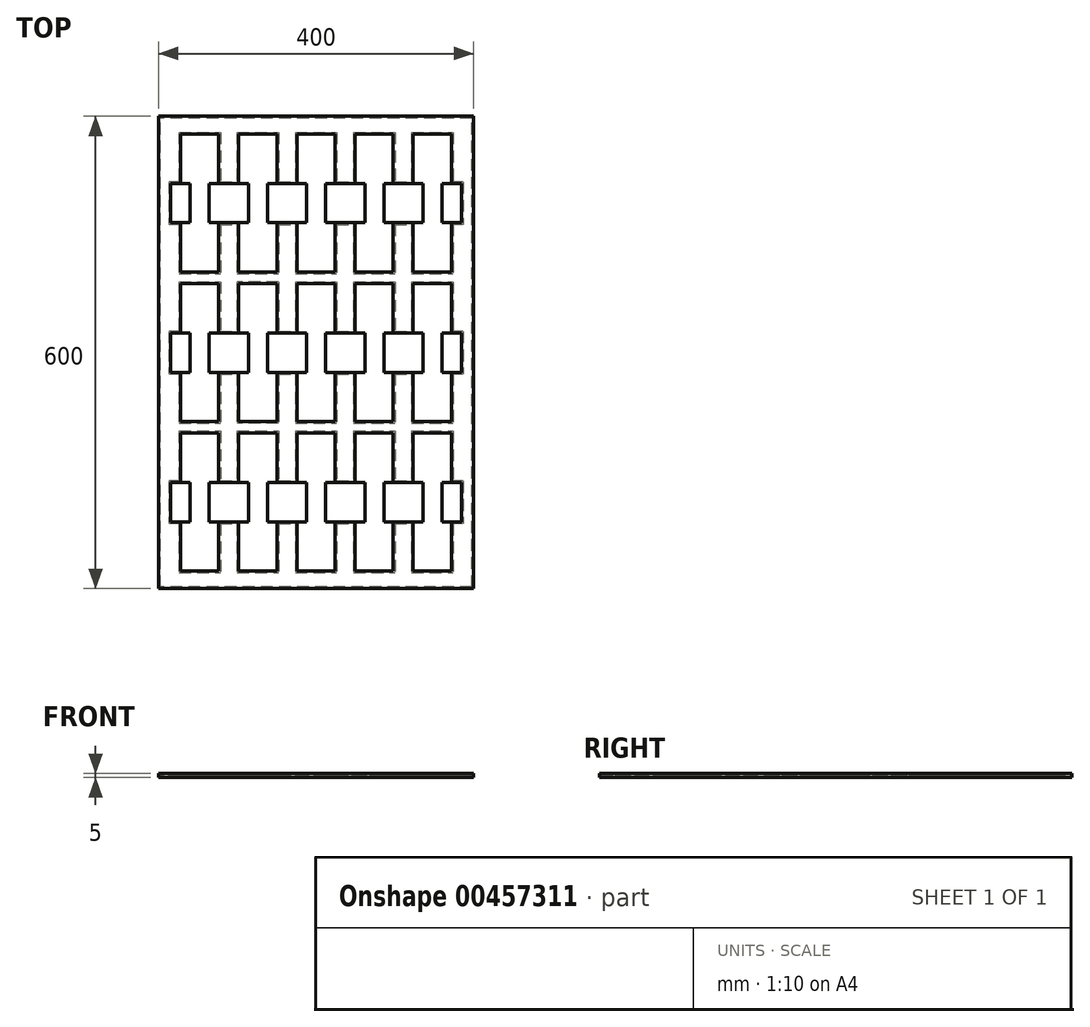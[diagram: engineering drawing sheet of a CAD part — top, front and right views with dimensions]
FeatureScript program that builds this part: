
annotation { "Feature Type Name" : "Feature", "Feature Type Description" : "" }
export const myFeature = defineFeature(function(context is Context, id is Id, definition is map)
    precondition{}
    {
        {
            var Q0;
            Q0=qCreatedBy(makeId("Top.planeOp"),FACE);
            var sketch = newSketch(context, id + "F0", { "sketchPlane" : qUnion([Q0])});
            skLineSegment(sketch, "E0.bottom", {"start": v(200, -300) * mm, "end": v(-200, -300) * mm});
            skLineSegment(sketch, "E0.top", {"start": v(200, 300) * mm, "end": v(-200, 300) * mm});
            skLineSegment(sketch, "E0.left", {"start": v(200, -300) * mm, "end": v(200, 300) * mm});
            skLineSegment(sketch, "E0.right", {"start": v(-200, -300) * mm, "end": v(-200, 300) * mm});
            skPoint(sketch, "E0.middle", {"position": v(0, 0) * mm});
            skSolve(sketch);
        }
        {
            var Q0;
            Q0 = qSketchRegion(id + "F0", true);
            extrude(context, id + "F1", {"entities" : qUnion([Q0]), "depth" : 2 * mm});
        }
        {
            var Q0;
            Q0=makeQuery(id+"F1.opExtrude","CAP_FACE",FACE,{"disambiguationData":[OSD([sQuery(id+"F0.wireOp",EDGE,"E0.bottom"),sQuery(id+"F0.wireOp",EDGE,"E0.top"),sQuery(id+"F0.wireOp",EDGE,"E0.left"),sQuery(id+"F0.wireOp",EDGE,"E0.right")])],"isStart":false});
            var sketch = newSketch(context, id + "F2", { "sketchPlane" : qUnion([Q0])});
            skLineSegment(sketch, "E1.bottom", {"start": v(-172, 277.5) * mm, "end": v(-123.5, 277.5) * mm});
            skLineSegment(sketch, "E1.top", {"start": v(-172, 102) * mm, "end": v(-123.5, 102) * mm});
            skLineSegment(sketch, "E1.left", {"start": v(-172, 277.5) * mm, "end": v(-172, 102) * mm});
            skLineSegment(sketch, "E1.right", {"start": v(-123.5, 277.5) * mm, "end": v(-123.5, 102) * mm});
            skLineSegment(sketch, "E2.0.1.0", {"start": v(-172, 87.75) * mm, "end": v(-123.5, 87.75) * mm});
            skLineSegment(sketch, "E2.0.1.1", {"start": v(-123.5, 87.75) * mm, "end": v(-123.5, -87.75) * mm});
            skLineSegment(sketch, "E2.0.1.2", {"start": v(-172, -87.75) * mm, "end": v(-123.5, -87.75) * mm});
            skLineSegment(sketch, "E2.0.1.3", {"start": v(-172, 87.75) * mm, "end": v(-172, -87.75) * mm});
            skLineSegment(sketch, "E2.0.2.0", {"start": v(-172, -102) * mm, "end": v(-123.5, -102) * mm});
            skLineSegment(sketch, "E2.0.2.1", {"start": v(-123.5, -102) * mm, "end": v(-123.5, -277.5) * mm});
            skLineSegment(sketch, "E2.0.2.2", {"start": v(-172, -277.5) * mm, "end": v(-123.5, -277.5) * mm});
            skLineSegment(sketch, "E2.0.2.3", {"start": v(-172, -102) * mm, "end": v(-172, -277.5) * mm});
            skLineSegment(sketch, "E2.1.0.0", {"start": v(-98.13, 277.5) * mm, "end": v(-49.63, 277.5) * mm});
            skLineSegment(sketch, "E2.1.0.1", {"start": v(-49.63, 277.5) * mm, "end": v(-49.63, 102) * mm});
            skLineSegment(sketch, "E2.1.0.2", {"start": v(-98.13, 102) * mm, "end": v(-49.63, 102) * mm});
            skLineSegment(sketch, "E2.1.0.3", {"start": v(-98.13, 277.5) * mm, "end": v(-98.13, 102) * mm});
            skLineSegment(sketch, "E2.1.1.0", {"start": v(-98.13, 87.75) * mm, "end": v(-49.63, 87.75) * mm});
            skLineSegment(sketch, "E2.1.1.1", {"start": v(-49.63, 87.75) * mm, "end": v(-49.63, -87.75) * mm});
            skLineSegment(sketch, "E2.1.1.2", {"start": v(-98.13, -87.75) * mm, "end": v(-49.63, -87.75) * mm});
            skLineSegment(sketch, "E2.1.1.3", {"start": v(-98.13, 87.75) * mm, "end": v(-98.13, -87.75) * mm});
            skLineSegment(sketch, "E2.1.2.0", {"start": v(-98.13, -102) * mm, "end": v(-49.63, -102) * mm});
            skLineSegment(sketch, "E2.1.2.1", {"start": v(-49.63, -102) * mm, "end": v(-49.63, -277.5) * mm});
            skLineSegment(sketch, "E2.1.2.2", {"start": v(-98.13, -277.5) * mm, "end": v(-49.63, -277.5) * mm});
            skLineSegment(sketch, "E2.1.2.3", {"start": v(-98.13, -102) * mm, "end": v(-98.13, -277.5) * mm});
            skLineSegment(sketch, "E2.2.0.0", {"start": v(-24.25, 277.5) * mm, "end": v(24.25, 277.5) * mm});
            skLineSegment(sketch, "E2.2.0.1", {"start": v(24.25, 277.5) * mm, "end": v(24.25, 102) * mm});
            skLineSegment(sketch, "E2.2.0.2", {"start": v(-24.25, 102) * mm, "end": v(24.25, 102) * mm});
            skLineSegment(sketch, "E2.2.0.3", {"start": v(-24.25, 277.5) * mm, "end": v(-24.25, 102) * mm});
            skLineSegment(sketch, "E2.2.1.0", {"start": v(-24.25, 87.75) * mm, "end": v(24.25, 87.75) * mm});
            skLineSegment(sketch, "E2.2.1.1", {"start": v(24.25, 87.75) * mm, "end": v(24.25, -87.75) * mm});
            skLineSegment(sketch, "E2.2.1.2", {"start": v(-24.25, -87.75) * mm, "end": v(24.25, -87.75) * mm});
            skLineSegment(sketch, "E2.2.1.3", {"start": v(-24.25, 87.75) * mm, "end": v(-24.25, -87.75) * mm});
            skLineSegment(sketch, "E2.2.2.0", {"start": v(-24.25, -102) * mm, "end": v(24.25, -102) * mm});
            skLineSegment(sketch, "E2.2.2.1", {"start": v(24.25, -102) * mm, "end": v(24.25, -277.5) * mm});
            skLineSegment(sketch, "E2.2.2.2", {"start": v(-24.25, -277.5) * mm, "end": v(24.25, -277.5) * mm});
            skLineSegment(sketch, "E2.2.2.3", {"start": v(-24.25, -102) * mm, "end": v(-24.25, -277.5) * mm});
            skLineSegment(sketch, "E2.3.0.0", {"start": v(49.62, 277.5) * mm, "end": v(98.12, 277.5) * mm});
            skLineSegment(sketch, "E2.3.0.1", {"start": v(98.12, 277.5) * mm, "end": v(98.12, 102) * mm});
            skLineSegment(sketch, "E2.3.0.2", {"start": v(49.62, 102) * mm, "end": v(98.12, 102) * mm});
            skLineSegment(sketch, "E2.3.0.3", {"start": v(49.62, 277.5) * mm, "end": v(49.62, 102) * mm});
            skLineSegment(sketch, "E2.3.1.0", {"start": v(49.62, 87.75) * mm, "end": v(98.12, 87.75) * mm});
            skLineSegment(sketch, "E2.3.1.1", {"start": v(98.12, 87.75) * mm, "end": v(98.12, -87.75) * mm});
            skLineSegment(sketch, "E2.3.1.2", {"start": v(49.62, -87.75) * mm, "end": v(98.12, -87.75) * mm});
            skLineSegment(sketch, "E2.3.1.3", {"start": v(49.62, 87.75) * mm, "end": v(49.62, -87.75) * mm});
            skLineSegment(sketch, "E2.3.2.0", {"start": v(49.62, -102) * mm, "end": v(98.12, -102) * mm});
            skLineSegment(sketch, "E2.3.2.1", {"start": v(98.12, -102) * mm, "end": v(98.12, -277.5) * mm});
            skLineSegment(sketch, "E2.3.2.2", {"start": v(49.62, -277.5) * mm, "end": v(98.12, -277.5) * mm});
            skLineSegment(sketch, "E2.3.2.3", {"start": v(49.62, -102) * mm, "end": v(49.62, -277.5) * mm});
            skLineSegment(sketch, "E2.4.0.0", {"start": v(123.5, 277.5) * mm, "end": v(172, 277.5) * mm});
            skLineSegment(sketch, "E2.4.0.1", {"start": v(172, 277.5) * mm, "end": v(172, 102) * mm});
            skLineSegment(sketch, "E2.4.0.2", {"start": v(123.5, 102) * mm, "end": v(172, 102) * mm});
            skLineSegment(sketch, "E2.4.0.3", {"start": v(123.5, 277.5) * mm, "end": v(123.5, 102) * mm});
            skLineSegment(sketch, "E2.4.1.0", {"start": v(123.5, 87.75) * mm, "end": v(172, 87.75) * mm});
            skLineSegment(sketch, "E2.4.1.1", {"start": v(172, 87.75) * mm, "end": v(172, -87.75) * mm});
            skLineSegment(sketch, "E2.4.1.2", {"start": v(123.5, -87.75) * mm, "end": v(172, -87.75) * mm});
            skLineSegment(sketch, "E2.4.1.3", {"start": v(123.5, 87.75) * mm, "end": v(123.5, -87.75) * mm});
            skLineSegment(sketch, "E2.4.2.0", {"start": v(123.5, -102) * mm, "end": v(172, -102) * mm});
            skLineSegment(sketch, "E2.4.2.1", {"start": v(172, -102) * mm, "end": v(172, -277.5) * mm});
            skLineSegment(sketch, "E2.4.2.2", {"start": v(123.5, -277.5) * mm, "end": v(172, -277.5) * mm});
            skLineSegment(sketch, "E2.4.2.3", {"start": v(123.5, -102) * mm, "end": v(123.5, -277.5) * mm});
            skLineSegment(sketch, "E3", {"start": v(-333.48, 0) * mm, "end": v(360.99, 0) * mm, "construction": true});
            skLineSegment(sketch, "E4", {"start": v(0, 318.35) * mm, "end": v(-24.25, -9048.14) * mm, "construction": true});
            skLineSegment(sketch, "E5.bottom", {"start": v(-200, 300) * mm, "end": v(200, 300) * mm});
            skLineSegment(sketch, "E5.top", {"start": v(-200, -300) * mm, "end": v(200, -300) * mm});
            skLineSegment(sketch, "E5.left", {"start": v(-200, 300) * mm, "end": v(-200, -300) * mm});
            skLineSegment(sketch, "E5.right", {"start": v(200, 300) * mm, "end": v(200, -300) * mm});
            skSolve(sketch);
        }
        {
            var Q0;
            Q0 = qSketchRegion(id + "F2", true);
            extrude(context, id + "F3", {"entities" : qUnion([Q0]), "operationType" : NewBodyOperationType.ADD, "depth" : 3 * mm});
        }
        {
            var Q0;
            Q0=makeQuery(id+"F3.opExtrude","CAP_FACE",FACE,{"disambiguationData":[OSD([sQuery(id+"F2.wireOp",EDGE,"E1.top"),sQuery(id+"F2.wireOp",EDGE,"E1.right"),sQuery(id+"F2.wireOp",EDGE,"E2.0.1.0"),sQuery(id+"F2.wireOp",EDGE,"E2.0.1.1"),sQuery(id+"F2.wireOp",EDGE,"E2.0.1.2"),sQuery(id+"F2.wireOp",EDGE,"E2.0.1.3"),sQuery(id+"F2.wireOp",EDGE,"E2.0.2.0"),sQuery(id+"F2.wireOp",EDGE,"E2.0.2.1"),sQuery(id+"F2.wireOp",EDGE,"E2.0.2.2"),sQuery(id+"F2.wireOp",EDGE,"E2.0.2.3"),sQuery(id+"F2.wireOp",EDGE,"E2.1.0.0"),sQuery(id+"F2.wireOp",EDGE,"E2.1.0.1"),sQuery(id+"F2.wireOp",EDGE,"E2.1.0.2"),sQuery(id+"F2.wireOp",EDGE,"E2.1.0.3"),sQuery(id+"F2.wireOp",EDGE,"E2.1.1.0"),sQuery(id+"F2.wireOp",EDGE,"E2.1.1.1"),sQuery(id+"F2.wireOp",EDGE,"E2.1.1.2"),sQuery(id+"F2.wireOp",EDGE,"E2.1.1.3"),sQuery(id+"F2.wireOp",EDGE,"E2.1.2.0"),sQuery(id+"F2.wireOp",EDGE,"E2.1.2.1"),sQuery(id+"F2.wireOp",EDGE,"E2.1.2.2"),sQuery(id+"F2.wireOp",EDGE,"E2.1.2.3"),sQuery(id+"F2.wireOp",EDGE,"E2.2.0.0"),sQuery(id+"F2.wireOp",EDGE,"E2.2.0.1"),sQuery(id+"F2.wireOp",EDGE,"E2.2.0.2"),sQuery(id+"F2.wireOp",EDGE,"E2.2.0.3"),sQuery(id+"F2.wireOp",EDGE,"E2.2.1.0"),sQuery(id+"F2.wireOp",EDGE,"E2.2.1.1"),sQuery(id+"F2.wireOp",EDGE,"E2.2.1.2"),sQuery(id+"F2.wireOp",EDGE,"E2.2.1.3"),sQuery(id+"F2.wireOp",EDGE,"E2.2.2.0"),sQuery(id+"F2.wireOp",EDGE,"E2.2.2.1"),sQuery(id+"F2.wireOp",EDGE,"E2.2.2.2"),sQuery(id+"F2.wireOp",EDGE,"E2.2.2.3"),sQuery(id+"F2.wireOp",EDGE,"E2.3.0.0"),sQuery(id+"F2.wireOp",EDGE,"E2.3.0.1"),sQuery(id+"F2.wireOp",EDGE,"E2.3.0.2"),sQuery(id+"F2.wireOp",EDGE,"E2.3.0.3"),sQuery(id+"F2.wireOp",EDGE,"E2.3.1.0"),sQuery(id+"F2.wireOp",EDGE,"E2.3.1.1"),sQuery(id+"F2.wireOp",EDGE,"E2.3.1.2"),sQuery(id+"F2.wireOp",EDGE,"E2.3.1.3"),sQuery(id+"F2.wireOp",EDGE,"E2.3.2.0"),sQuery(id+"F2.wireOp",EDGE,"E2.3.2.1"),sQuery(id+"F2.wireOp",EDGE,"E2.3.2.2"),sQuery(id+"F2.wireOp",EDGE,"E2.3.2.3"),sQuery(id+"F2.wireOp",EDGE,"E2.4.0.0"),sQuery(id+"F2.wireOp",EDGE,"E2.4.0.1"),sQuery(id+"F2.wireOp",EDGE,"E2.4.0.2"),sQuery(id+"F2.wireOp",EDGE,"E2.4.0.3"),sQuery(id+"F2.wireOp",EDGE,"E2.4.1.0"),sQuery(id+"F2.wireOp",EDGE,"E2.4.1.1"),sQuery(id+"F2.wireOp",EDGE,"E2.4.1.2"),sQuery(id+"F2.wireOp",EDGE,"E2.4.1.3"),sQuery(id+"F2.wireOp",EDGE,"E2.4.2.0"),sQuery(id+"F2.wireOp",EDGE,"E2.4.2.1"),sQuery(id+"F2.wireOp",EDGE,"E2.4.2.2"),sQuery(id+"F2.wireOp",EDGE,"E2.4.2.3"),sQuery(id+"F2.wireOp",EDGE,"E1.bottom"),sQuery(id+"F2.wireOp",EDGE,"E1.left"),sQuery(id+"F2.wireOp",EDGE,"E5.bottom"),sQuery(id+"F2.wireOp",EDGE,"E5.top"),sQuery(id+"F2.wireOp",EDGE,"E5.left"),sQuery(id+"F2.wireOp",EDGE,"E5.right")])],"isStart":false});
            var sketch = newSketch(context, id + "F4", { "sketchPlane" : qUnion([Q0])});
            skLineSegment(sketch, "E6.bottom", {"start": v(-135.81, 164.75) * mm, "end": v(-85.81, 164.75) * mm});
            skLineSegment(sketch, "E6.top", {"start": v(-135.81, 214.75) * mm, "end": v(-85.81, 214.75) * mm});
            skLineSegment(sketch, "E6.left", {"start": v(-135.81, 164.75) * mm, "end": v(-135.81, 214.75) * mm});
            skLineSegment(sketch, "E6.right", {"start": v(-85.81, 164.75) * mm, "end": v(-85.81, 214.75) * mm});
            skLineSegment(sketch, "E7", {"start": v(-110.81, 237.25) * mm, "end": v(-110.81, 132.57) * mm, "construction": true});
            skLineSegment(sketch, "E8", {"start": v(-222.43, 189.75) * mm, "end": v(260.4, 189.75) * mm, "construction": true});
            skPoint(sketch, "E8.endSnap0", {"position": v(-98.13, 189.75) * mm});
            skLineSegment(sketch, "E9", {"start": v(-36.94, 239.15) * mm, "end": v(-36.94, 137.64) * mm, "construction": true});
            skLineSegment(sketch, "E10", {"start": v(-262.44, 94.87) * mm, "end": v(281.55, 94.87) * mm, "construction": true});
            skLineSegment(sketch, "E11", {"start": v(-247.35, -94.88) * mm, "end": v(283.81, -94.87) * mm, "construction": true});
            skLineSegment(sketch, "E12.0.1.0", {"start": v(-85.81, -25.25) * mm, "end": v(-85.81, 24.75) * mm});
            skLineSegment(sketch, "E12.0.1.1", {"start": v(-135.81, 24.75) * mm, "end": v(-85.81, 24.75) * mm});
            skLineSegment(sketch, "E12.0.1.2", {"start": v(-135.81, -25.25) * mm, "end": v(-135.81, 24.75) * mm});
            skLineSegment(sketch, "E12.0.1.3", {"start": v(-110.81, 47.25) * mm, "end": v(-110.81, -57.43) * mm, "construction": true});
            skLineSegment(sketch, "E12.0.1.4", {"start": v(-135.81, -25.25) * mm, "end": v(-85.81, -25.25) * mm});
            skLineSegment(sketch, "E12.0.2.0", {"start": v(-85.81, -215.25) * mm, "end": v(-85.81, -165.25) * mm});
            skLineSegment(sketch, "E12.0.2.1", {"start": v(-135.81, -165.25) * mm, "end": v(-85.81, -165.25) * mm});
            skLineSegment(sketch, "E12.0.2.2", {"start": v(-135.81, -215.25) * mm, "end": v(-135.81, -165.25) * mm});
            skLineSegment(sketch, "E12.0.2.3", {"start": v(-110.81, -142.75) * mm, "end": v(-110.81, -247.43) * mm, "construction": true});
            skLineSegment(sketch, "E12.0.2.4", {"start": v(-135.81, -215.25) * mm, "end": v(-85.81, -215.25) * mm});
            skLineSegment(sketch, "E12.1.0.0", {"start": v(-11.81, 164.75) * mm, "end": v(-11.81, 214.75) * mm});
            skLineSegment(sketch, "E12.1.0.1", {"start": v(-61.81, 214.75) * mm, "end": v(-11.81, 214.75) * mm});
            skLineSegment(sketch, "E12.1.0.2", {"start": v(-61.81, 164.75) * mm, "end": v(-61.81, 214.75) * mm});
            skLineSegment(sketch, "E12.1.0.3", {"start": v(-36.81, 237.25) * mm, "end": v(-36.81, 132.57) * mm, "construction": true});
            skLineSegment(sketch, "E12.1.0.4", {"start": v(-61.81, 164.75) * mm, "end": v(-11.81, 164.75) * mm});
            skLineSegment(sketch, "E12.1.1.0", {"start": v(-11.81, -25.25) * mm, "end": v(-11.81, 24.75) * mm});
            skLineSegment(sketch, "E12.1.1.1", {"start": v(-61.81, 24.75) * mm, "end": v(-11.81, 24.75) * mm});
            skLineSegment(sketch, "E12.1.1.2", {"start": v(-61.81, -25.25) * mm, "end": v(-61.81, 24.75) * mm});
            skLineSegment(sketch, "E12.1.1.3", {"start": v(-36.81, 47.25) * mm, "end": v(-36.81, -57.43) * mm, "construction": true});
            skLineSegment(sketch, "E12.1.1.4", {"start": v(-61.81, -25.25) * mm, "end": v(-11.81, -25.25) * mm});
            skLineSegment(sketch, "E12.1.2.0", {"start": v(-11.81, -215.25) * mm, "end": v(-11.81, -165.25) * mm});
            skLineSegment(sketch, "E12.1.2.1", {"start": v(-61.81, -165.25) * mm, "end": v(-11.81, -165.25) * mm});
            skLineSegment(sketch, "E12.1.2.2", {"start": v(-61.81, -215.25) * mm, "end": v(-61.81, -165.25) * mm});
            skLineSegment(sketch, "E12.1.2.3", {"start": v(-36.81, -142.75) * mm, "end": v(-36.81, -247.43) * mm, "construction": true});
            skLineSegment(sketch, "E12.1.2.4", {"start": v(-61.81, -215.25) * mm, "end": v(-11.81, -215.25) * mm});
            skLineSegment(sketch, "E12.2.0.0", {"start": v(62.19, 164.75) * mm, "end": v(62.19, 214.75) * mm});
            skLineSegment(sketch, "E12.2.0.1", {"start": v(12.19, 214.75) * mm, "end": v(62.19, 214.75) * mm});
            skLineSegment(sketch, "E12.2.0.2", {"start": v(12.19, 164.75) * mm, "end": v(12.19, 214.75) * mm});
            skLineSegment(sketch, "E12.2.0.3", {"start": v(37.19, 237.25) * mm, "end": v(37.19, 132.57) * mm, "construction": true});
            skLineSegment(sketch, "E12.2.0.4", {"start": v(12.19, 164.75) * mm, "end": v(62.19, 164.75) * mm});
            skLineSegment(sketch, "E12.2.1.0", {"start": v(62.19, -25.25) * mm, "end": v(62.19, 24.75) * mm});
            skLineSegment(sketch, "E12.2.1.1", {"start": v(12.19, 24.75) * mm, "end": v(62.19, 24.75) * mm});
            skLineSegment(sketch, "E12.2.1.2", {"start": v(12.19, -25.25) * mm, "end": v(12.19, 24.75) * mm});
            skLineSegment(sketch, "E12.2.1.3", {"start": v(37.19, 47.25) * mm, "end": v(37.19, -57.43) * mm, "construction": true});
            skLineSegment(sketch, "E12.2.1.4", {"start": v(12.19, -25.25) * mm, "end": v(62.19, -25.25) * mm});
            skLineSegment(sketch, "E12.2.2.0", {"start": v(62.19, -215.25) * mm, "end": v(62.19, -165.25) * mm});
            skLineSegment(sketch, "E12.2.2.1", {"start": v(12.19, -165.25) * mm, "end": v(62.19, -165.25) * mm});
            skLineSegment(sketch, "E12.2.2.2", {"start": v(12.19, -215.25) * mm, "end": v(12.19, -165.25) * mm});
            skLineSegment(sketch, "E12.2.2.3", {"start": v(37.19, -142.75) * mm, "end": v(37.19, -247.43) * mm, "construction": true});
            skLineSegment(sketch, "E12.2.2.4", {"start": v(12.19, -215.25) * mm, "end": v(62.19, -215.25) * mm});
            skLineSegment(sketch, "E12.3.0.0", {"start": v(136.19, 164.75) * mm, "end": v(136.19, 214.75) * mm});
            skLineSegment(sketch, "E12.3.0.1", {"start": v(86.19, 214.75) * mm, "end": v(136.19, 214.75) * mm});
            skLineSegment(sketch, "E12.3.0.2", {"start": v(86.19, 164.75) * mm, "end": v(86.19, 214.75) * mm});
            skLineSegment(sketch, "E12.3.0.3", {"start": v(111.19, 237.25) * mm, "end": v(111.19, 132.57) * mm, "construction": true});
            skLineSegment(sketch, "E12.3.0.4", {"start": v(86.19, 164.75) * mm, "end": v(136.19, 164.75) * mm});
            skLineSegment(sketch, "E12.3.1.0", {"start": v(136.19, -25.25) * mm, "end": v(136.19, 24.75) * mm});
            skLineSegment(sketch, "E12.3.1.1", {"start": v(86.19, 24.75) * mm, "end": v(136.19, 24.75) * mm});
            skLineSegment(sketch, "E12.3.1.2", {"start": v(86.19, -25.25) * mm, "end": v(86.19, 24.75) * mm});
            skLineSegment(sketch, "E12.3.1.3", {"start": v(111.19, 47.25) * mm, "end": v(111.19, -57.43) * mm, "construction": true});
            skLineSegment(sketch, "E12.3.1.4", {"start": v(86.19, -25.25) * mm, "end": v(136.19, -25.25) * mm});
            skLineSegment(sketch, "E12.3.2.0", {"start": v(136.19, -215.25) * mm, "end": v(136.19, -165.25) * mm});
            skLineSegment(sketch, "E12.3.2.1", {"start": v(86.19, -165.25) * mm, "end": v(136.19, -165.25) * mm});
            skLineSegment(sketch, "E12.3.2.2", {"start": v(86.19, -215.25) * mm, "end": v(86.19, -165.25) * mm});
            skLineSegment(sketch, "E12.3.2.3", {"start": v(111.19, -142.75) * mm, "end": v(111.19, -247.43) * mm, "construction": true});
            skLineSegment(sketch, "E12.3.2.4", {"start": v(86.19, -215.25) * mm, "end": v(136.19, -215.25) * mm});
            skLineSegment(sketch, "E12.direction1", {"start": v(-85.81, 164.75) * mm, "end": v(-11.81, 164.75) * mm, "construction": true});
            skLineSegment(sketch, "E12.direction2", {"start": v(-85.81, 164.75) * mm, "end": v(-85.81, -25.25) * mm, "construction": true});
            skLineSegment(sketch, "E13.bottom", {"start": v(-159.69, 214.75) * mm, "end": v(-184.69, 214.75) * mm});
            skLineSegment(sketch, "E13.top", {"start": v(-159.69, 164.75) * mm, "end": v(-184.69, 164.75) * mm});
            skLineSegment(sketch, "E13.left", {"start": v(-159.69, 214.75) * mm, "end": v(-159.69, 164.75) * mm});
            skLineSegment(sketch, "E13.right", {"start": v(-184.69, 214.75) * mm, "end": v(-184.69, 164.75) * mm});
            skLineSegment(sketch, "E14", {"start": v(-147.75, 140.31) * mm, "end": v(-147.75, 261.03) * mm, "construction": true});
            skLineSegment(sketch, "E15.0.1.0", {"start": v(-159.69, -25.25) * mm, "end": v(-184.69, -25.25) * mm});
            skLineSegment(sketch, "E15.0.1.1", {"start": v(-159.69, 24.75) * mm, "end": v(-184.69, 24.75) * mm});
            skLineSegment(sketch, "E15.0.1.2", {"start": v(-159.69, 24.75) * mm, "end": v(-159.69, -25.25) * mm});
            skLineSegment(sketch, "E15.0.1.3", {"start": v(-184.69, 24.75) * mm, "end": v(-184.69, -25.25) * mm});
            skLineSegment(sketch, "E15.1.0.0", {"start": v(185, 164.75) * mm, "end": v(160, 164.75) * mm});
            skLineSegment(sketch, "E15.1.0.1", {"start": v(185, 214.75) * mm, "end": v(160, 214.75) * mm});
            skLineSegment(sketch, "E15.1.0.2", {"start": v(185, 214.75) * mm, "end": v(185, 164.75) * mm});
            skLineSegment(sketch, "E15.1.0.3", {"start": v(160, 214.75) * mm, "end": v(160, 164.75) * mm});
            skLineSegment(sketch, "E15.1.1.0", {"start": v(185, -25.25) * mm, "end": v(160, -25.25) * mm});
            skLineSegment(sketch, "E15.1.1.1", {"start": v(185, 24.75) * mm, "end": v(160, 24.75) * mm});
            skLineSegment(sketch, "E15.1.1.2", {"start": v(185, 24.75) * mm, "end": v(185, -25.25) * mm});
            skLineSegment(sketch, "E15.1.1.3", {"start": v(160, 24.75) * mm, "end": v(160, -25.25) * mm});
            skLineSegment(sketch, "E15.direction1", {"start": v(-184.69, 164.75) * mm, "end": v(160, 164.75) * mm, "construction": true});
            skLineSegment(sketch, "E15.direction2", {"start": v(-184.69, 164.75) * mm, "end": v(-184.69, -25.25) * mm, "construction": true});
            skLineSegment(sketch, "E16.0.0.2", {"start": v(-159.69, -215.25) * mm, "end": v(-184.69, -215.25) * mm});
            skLineSegment(sketch, "E16.3.0.2", {"start": v(-159.69, -165.25) * mm, "end": v(-184.69, -165.25) * mm});
            skLineSegment(sketch, "E16.6.0.2", {"start": v(-159.69, -165.25) * mm, "end": v(-159.69, -215.25) * mm});
            skLineSegment(sketch, "E16.9.0.2", {"start": v(-184.69, -165.25) * mm, "end": v(-184.69, -215.25) * mm});
            skLineSegment(sketch, "E16.0.1.2", {"start": v(185, -215.25) * mm, "end": v(160, -215.25) * mm});
            skLineSegment(sketch, "E16.3.1.2", {"start": v(185, -165.25) * mm, "end": v(160, -165.25) * mm});
            skLineSegment(sketch, "E16.6.1.2", {"start": v(185, -165.25) * mm, "end": v(185, -215.25) * mm});
            skLineSegment(sketch, "E16.9.1.2", {"start": v(160, -165.25) * mm, "end": v(160, -215.25) * mm});
            skSolve(sketch);
        }
        {
            var Q0;
            Q0 = qSketchRegion(id + "F4", true);
            extrude(context, id + "F5", {"entities" : qUnion([Q0]), "operationType" : NewBodyOperationType.REMOVE, "oppositeDirection" : true, "depth" : 25 * mm});
        }
        {
            var Q0;
            Q0=makeQuery(id+"F1.opExtrude","CAP_FACE",FACE,{"disambiguationData":[OSD([sQuery(id+"F0.wireOp",EDGE,"E0.bottom"),sQuery(id+"F0.wireOp",EDGE,"E0.top"),sQuery(id+"F0.wireOp",EDGE,"E0.left"),sQuery(id+"F0.wireOp",EDGE,"E0.right")])],"isStart":true});
            shell(context, id + "F6", {"entities" : qUnion([Q0]), "thickness" : 2 * mm});
        }
    });
